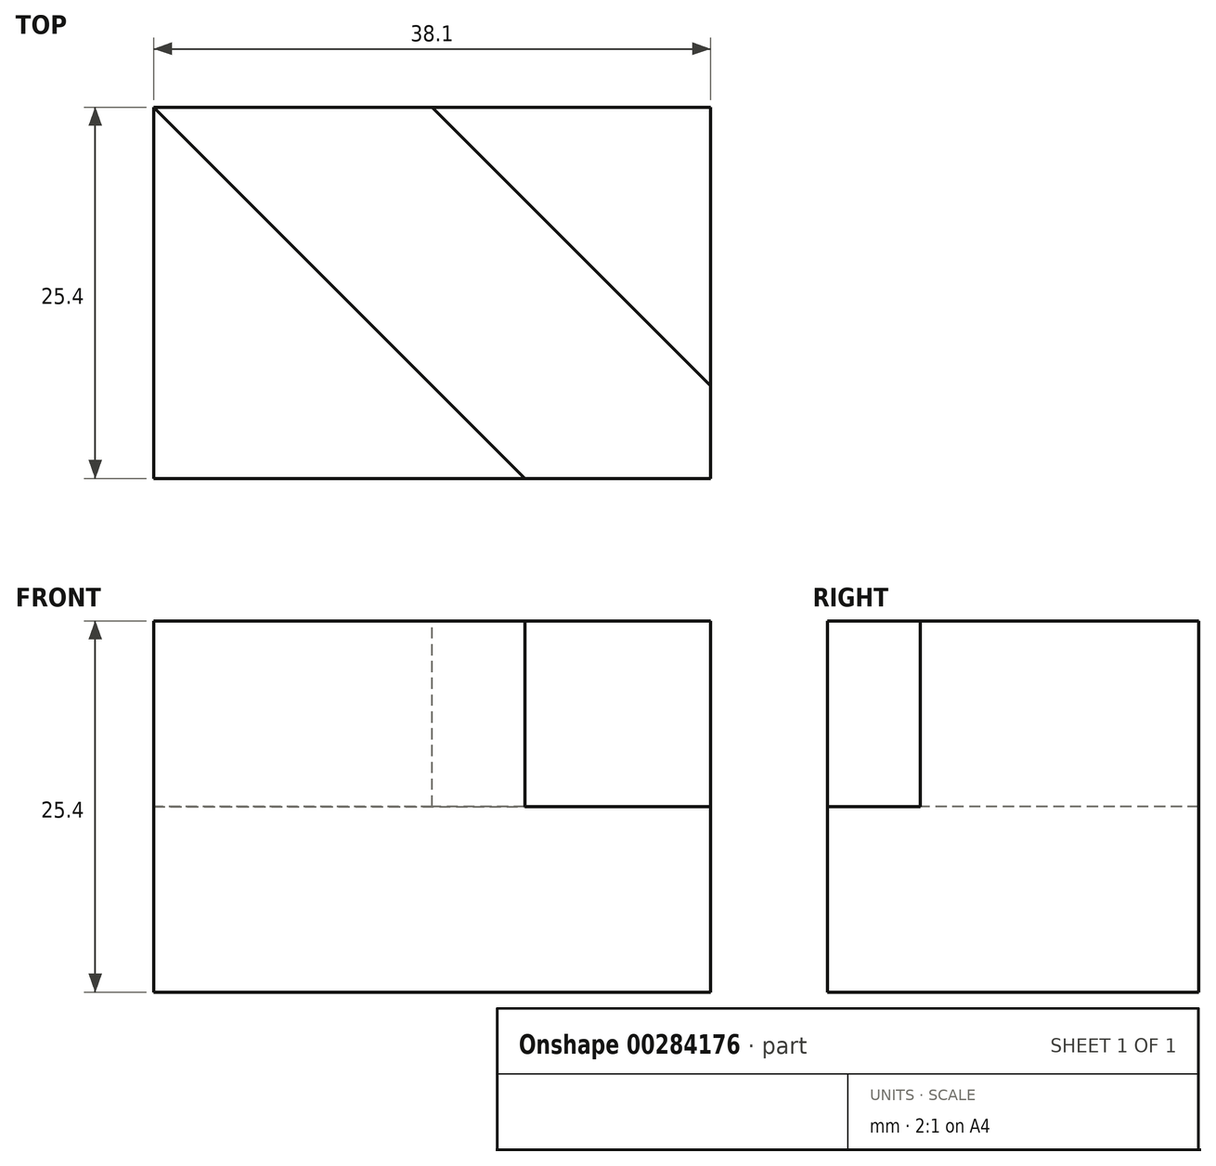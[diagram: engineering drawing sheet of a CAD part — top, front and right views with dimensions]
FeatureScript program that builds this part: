
annotation { "Feature Type Name" : "Feature", "Feature Type Description" : "" }
export const myFeature = defineFeature(function(context is Context, id is Id, definition is map)
    precondition{}
    {
        {
            var Q0;
            Q0=qCreatedBy(makeId("Top.planeOp"),FACE);
            var sketch = newSketch(context, id + "F0", { "sketchPlane" : qUnion([Q0])});
            skLineSegment(sketch, "E0.bottom", {"start": v(0, 25.4) * mm, "end": v(38.1, 25.4) * mm});
            skLineSegment(sketch, "E0.top", {"start": v(0, 0) * mm, "end": v(38.1, 0) * mm});
            skLineSegment(sketch, "E0.left", {"start": v(0, 25.4) * mm, "end": v(0, 0) * mm});
            skLineSegment(sketch, "E0.right", {"start": v(38.1, 25.4) * mm, "end": v(38.1, 0) * mm});
            skSolve(sketch);
        }
        {
            var Q0;
            Q0 = qSketchRegion(id + "F0", true);
            extrude(context, id + "F1", {"entities" : qUnion([Q0]), "oppositeDirection" : true, "depth" : 25.4 * mm});
        }
        {
            var Q0;
            Q0=qCreatedBy(makeId("Top.planeOp"),FACE);
            var sketch = newSketch(context, id + "F2", { "sketchPlane" : qUnion([Q0])});
            skLineSegment(sketch, "E1", {"start": v(0, 25.4) * mm, "end": v(25.4, 0) * mm});
            skLineSegment(sketch, "E2", {"start": v(25.4, 0) * mm, "end": v(38.1, 0) * mm});
            skLineSegment(sketch, "E3", {"start": v(38.1, 0) * mm, "end": v(38.1, 6.35) * mm});
            skLineSegment(sketch, "E4", {"start": v(38.1, 6.35) * mm, "end": v(19.05, 25.4) * mm});
            skLineSegment(sketch, "E5", {"start": v(19.05, 25.4) * mm, "end": v(0, 25.4) * mm});
            skSolve(sketch);
        }
        {
            var Q0;
            Q0 = qSketchRegion(id + "F2", true);
            extrude(context, id + "F3", {"entities" : qUnion([Q0]), "operationType" : NewBodyOperationType.REMOVE, "oppositeDirection" : true, "depth" : 12.7 * mm});
        }
    });
